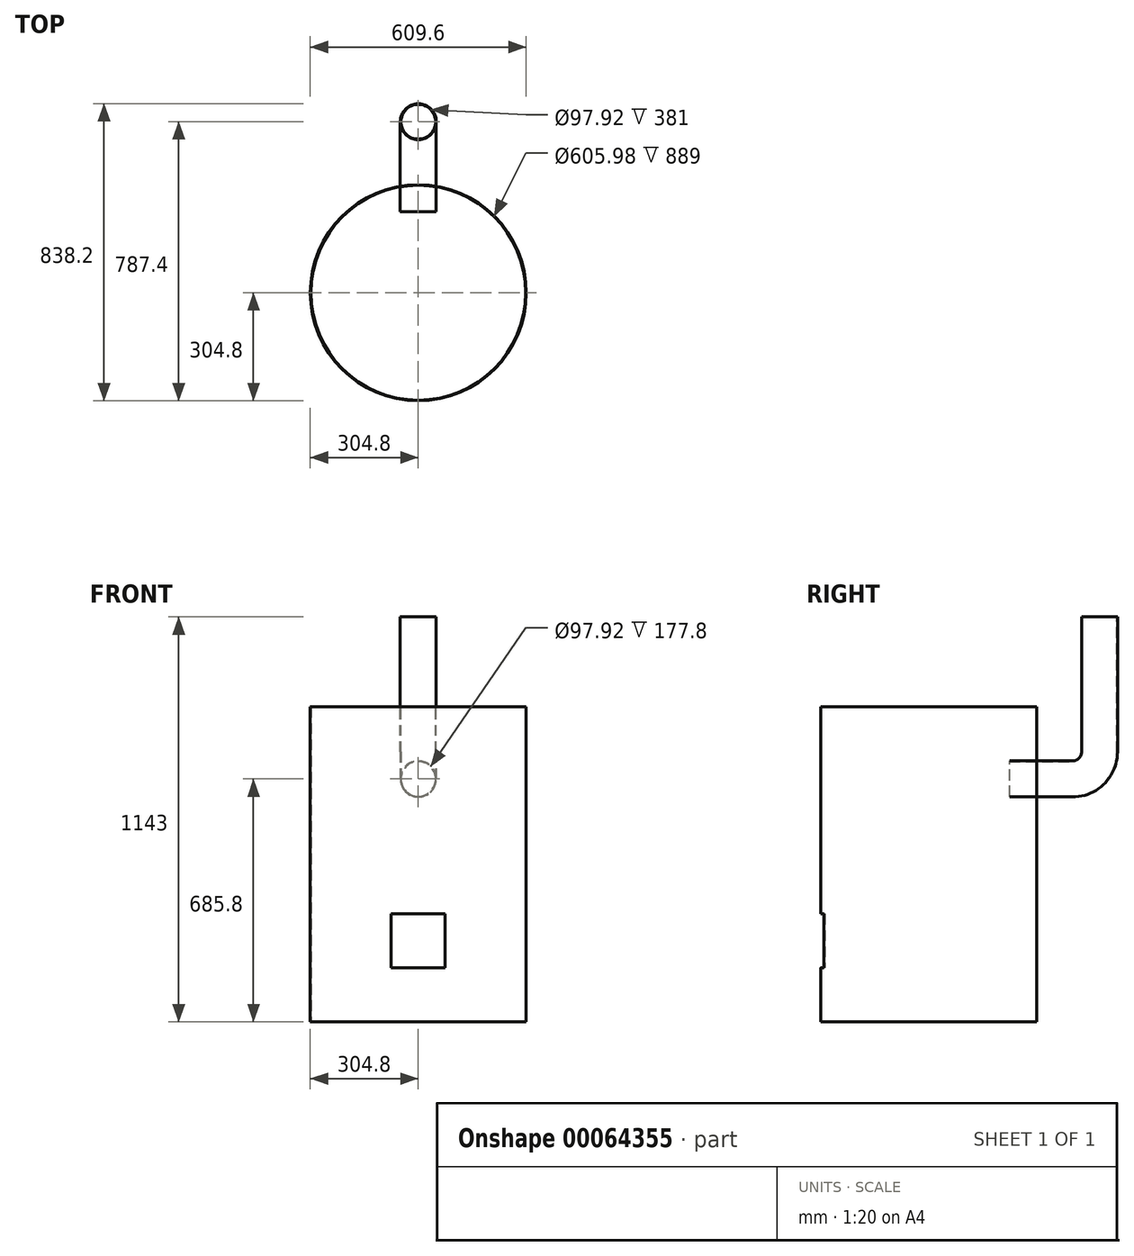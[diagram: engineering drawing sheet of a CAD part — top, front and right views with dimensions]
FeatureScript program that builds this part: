
annotation { "Feature Type Name" : "Feature", "Feature Type Description" : "" }
export const myFeature = defineFeature(function(context is Context, id is Id, definition is map)
    precondition{}
    {
        {
            var Q0;
            Q0=qCreatedBy(makeId("Top.planeOp"),FACE);
            var sketch = newSketch(context, id + "F0", { "sketchPlane" : qUnion([Q0])});
            skCircle(sketch, "E0", {"center": v(0, 0) * mm, "radius": 304.8 * mm});
            skCircle(sketch, "E1.0", {"center": v(0, 0) * mm, "radius": 303 * mm});
            skSolve(sketch);
        }
        {
            var Q0;
            Q0=makeQuery(id+"F0.imprint","IMPRINT",FACE,{"disambiguationData":[TD([[makeQuery(id+"F0.imprint","IMPRINT",EDGE,{"derivedFrom":sQuery(id+"F0.wireOp",EDGE,"E0")}),1.0]])]});
            extrude(context, id + "F1", {"entities" : qUnion([Q0]), "depth" : 889 * mm});
        }
        {
            var Q0;
            Q0=qCreatedBy(makeId("Front.planeOp"),FACE);
            cPlane(context, id + "F2", {"entities" : qUnion([Q0]), "cplaneType" : CPlaneType.OFFSET, "offset" : 304.8 * mm, "width" : 152.4 * mm, "height" : 152.4 * mm});
        }
        {
            var Q0;
            Q0=qCreatedBy(id+"F2.planeOp",FACE);
            var sketch = newSketch(context, id + "F3", { "sketchPlane" : qUnion([Q0])});
            skLineSegment(sketch, "E2", {"start": v(0, 0) * mm, "end": v(0, 228.6) * mm, "construction": true});
            skLineSegment(sketch, "E3.rect.bottom", {"start": v(76.2, 304.8) * mm, "end": v(-76.2, 304.8) * mm});
            skLineSegment(sketch, "E3.rect.top", {"start": v(76.2, 152.4) * mm, "end": v(-76.2, 152.4) * mm});
            skLineSegment(sketch, "E3.rect.left", {"start": v(76.2, 304.8) * mm, "end": v(76.2, 152.4) * mm});
            skLineSegment(sketch, "E3.rect.right", {"start": v(-76.2, 304.8) * mm, "end": v(-76.2, 152.4) * mm});
            skPoint(sketch, "E3.rect.middle", {"position": v(0, 228.6) * mm});
            skSolve(sketch);
        }
        {
            var Q0;
            Q0=makeQuery(id+"F3.imprint","IMPRINT",FACE,{"disambiguationData":[TD([[makeQuery(id+"F3.imprint","IMPRINT",EDGE,{"derivedFrom":sQuery(id+"F3.wireOp",EDGE,"E3.rect.bottom")}),1.0]])]});
            extrude(context, id + "F4", {"entities" : qUnion([Q0]), "operationType" : NewBodyOperationType.REMOVE, "oppositeDirection" : true, "depth" : 25.4 * mm});
        }
        {
            var Q0;
            Q0=qCreatedBy(makeId("Right.planeOp"),FACE);
            var sketch = newSketch(context, id + "F5", { "sketchPlane" : qUnion([Q0])});
            skLineSegment(sketch, "E4", {"start": v(0, 0) * mm, "end": v(0, 685.8) * mm, "construction": true});
            skLineSegment(sketch, "E5", {"start": v(228.6, 685.8) * mm, "end": v(406.4, 685.8) * mm});
            skLineSegment(sketch, "E6", {"start": v(482.6, 762) * mm, "end": v(482.6, 1143) * mm});
            skPoint(sketch, "E7.visualSharp", {"position": v(482.6, 685.8) * mm});
            skArc(sketch, "E7.filletArc", {"start": v(406.4, 685.8) * mm, "mid": v(460.28, 708.12) * mm, "end": v(482.6, 762) * mm});
            skSolve(sketch);
        }
        {
            var Q0;
            Q0=qCreatedBy(makeId("Front.planeOp"),FACE);
            cPlane(context, id + "F6", {"entities" : qUnion([Q0]), "cplaneType" : CPlaneType.OFFSET, "offset" : 228.6 * mm, "oppositeDirection" : true, "width" : 152.4 * mm, "height" : 152.4 * mm});
        }
        {
            var Q0;
            Q0=qCreatedBy(id+"F6.planeOp",FACE);
            var sketch = newSketch(context, id + "F7", { "sketchPlane" : qUnion([Q0])});
            skLineSegment(sketch, "E8.0", {"start": v(0, 0) * mm, "end": v(0, 685.8) * mm, "construction": true});
            skCircle(sketch, "E9", {"center": v(0, 685.8) * mm, "radius": 50.8 * mm});
            skCircle(sketch, "E10.0", {"center": v(0, 685.8) * mm, "radius": 48.96 * mm});
            skSolve(sketch);
        }
        {
            var Q0;
            Q0=makeQuery(id+"F7.imprint","IMPRINT",FACE,{"disambiguationData":[TD([[makeQuery(id+"F7.imprint","IMPRINT",EDGE,{"derivedFrom":sQuery(id+"F7.wireOp",EDGE,"E9")}),1.0]])]});
            var Q1;
            Q1=sQuery(id+"F5.wireOp",EDGE,"E5");
            var Q2;
            Q2=sQuery(id+"F5.wireOp",EDGE,"E7.filletArc");
            var Q3;
            Q3=sQuery(id+"F5.wireOp",EDGE,"E6");
            sweep(context, id + "F8", {"profiles" : qUnion([Q0]), "path" : qUnion([Q1, Q2, Q3])});
        }
    });
